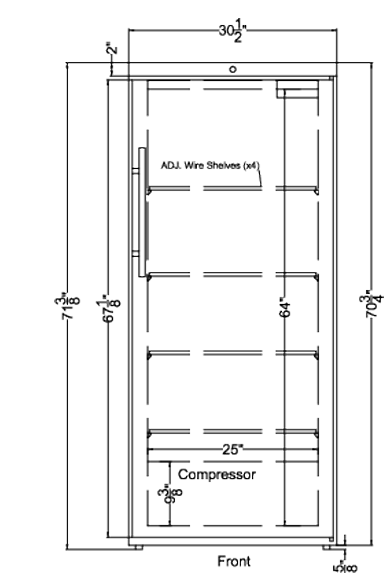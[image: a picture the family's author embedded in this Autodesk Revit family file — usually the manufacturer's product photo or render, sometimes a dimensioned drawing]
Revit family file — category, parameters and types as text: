
# Revit family: QF_Summit_UFM19W_Manual_Defrost_Freezer1
name_source: partatom
category: Specialty Equipment
units: mm (PartAtom-declared; Revit-internal decimal feet)

## family parameters
Always vertical = Yes
Cut with Voids When Loaded = No
Part Type = Normal
Room Calculation Point = No
Round Connector Dimension = Use Diameter
Shared = No
Work Plane-Based = No

## types (1)
- QF_Summit_UFM19W_Manual_Defrost_Freezer1
    Apparent Power = 0 VA
    BTUH = 0.0 Btu/h
    Conn Conduit = Yes
    Cycle = 60 Hz
    Default Elevation = 0"
    Depth = 27"
    Description = Manual Defrost Freezer
    Elec Conn Connection Height = 0"
    Elec Conn RI Height = 0"
    FL Amps = 3 A
    Foodservice Equipment Identifier = Yes
    Height = 71 3/8"
    Identify Quantity as Lot = Yes
    Length = 30 1/2"
    Manufacturer = Summit
    Max Overcurrent Protection = 0 A
    Min Ckt Ampacity = 0 A
    Model = UFM19W
    Number of Poles = 1
    Phase = 1
    Refrigerant Type = R290a
    Refrigerant Volume = 0.00 kip
    Volts = 115 V
    Watts = 311 W
    Weight in Pounds = 215

## geometry (parser evidence)
native form markers: Sweep x5
no freeform markers — native parametric forms only
